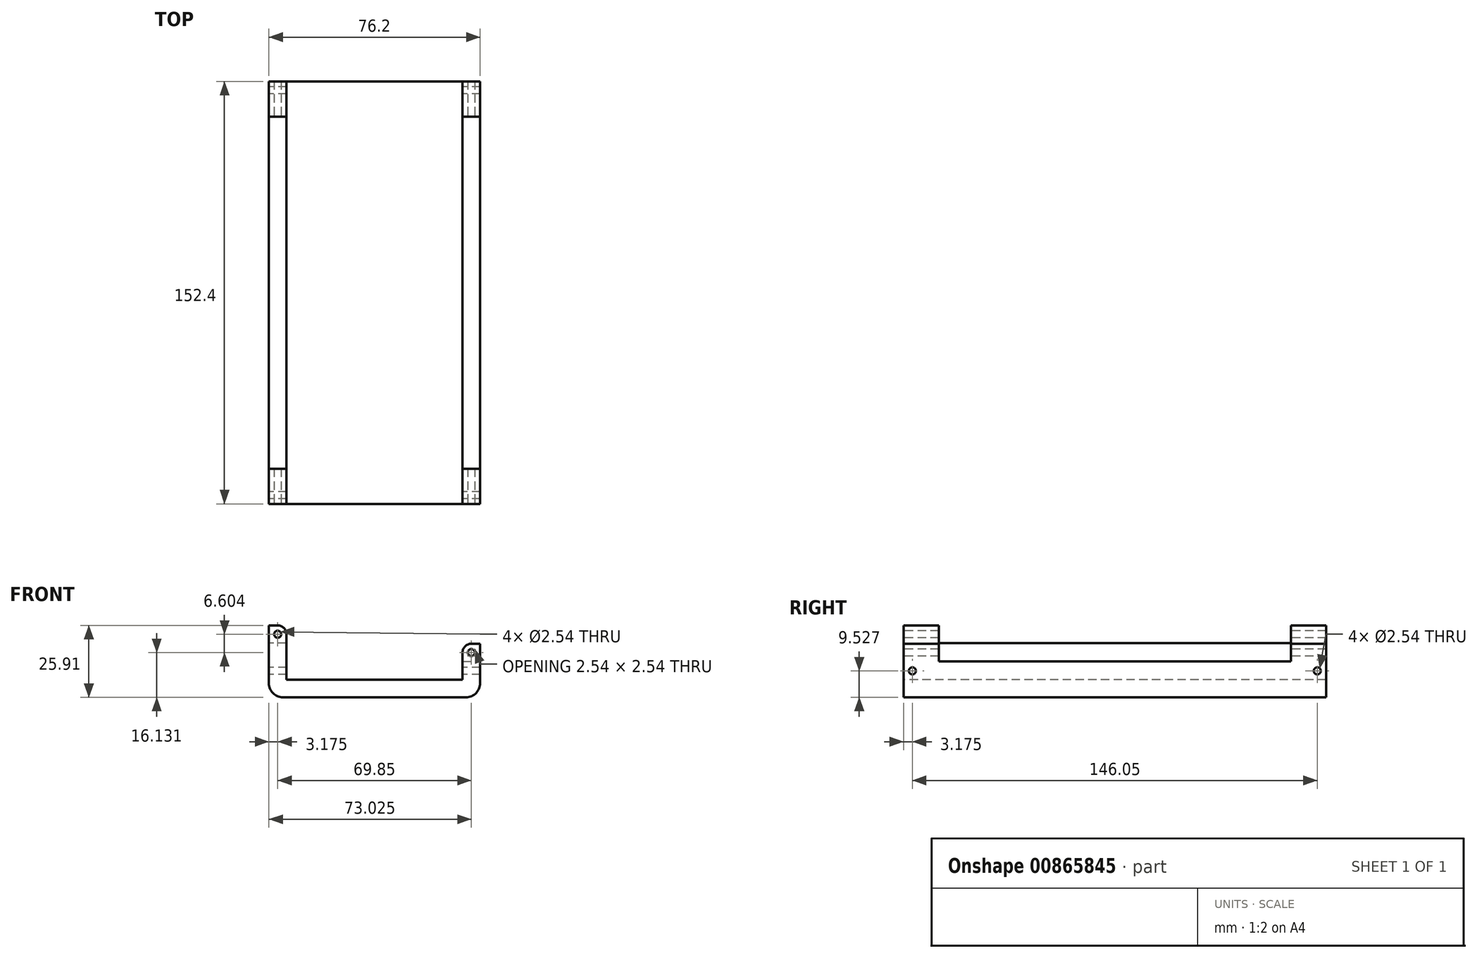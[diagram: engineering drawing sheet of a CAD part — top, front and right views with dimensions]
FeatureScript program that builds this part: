
annotation { "Feature Type Name" : "Feature", "Feature Type Description" : "" }
export const myFeature = defineFeature(function(context is Context, id is Id, definition is map)
    precondition{}
    {
        {
            var Q0;
            Q0=qCreatedBy(makeId("Front.planeOp"),FACE);
            var sketch = newSketch(context, id + "F0", { "sketchPlane" : qUnion([Q0])});
            skLineSegment(sketch, "E0", {"start": v(0, -19.56) * mm, "end": v(0, 0) * mm});
            skLineSegment(sketch, "E1", {"start": v(0, 0) * mm, "end": v(6.35, 0) * mm});
            skLineSegment(sketch, "E2", {"start": v(6.35, 0) * mm, "end": v(6.35, -13.2) * mm});
            skLineSegment(sketch, "E3", {"start": v(6.35, -13.2) * mm, "end": v(69.85, -13.2) * mm});
            skLineSegment(sketch, "E4", {"start": v(69.85, -13.2) * mm, "end": v(69.85, -6.6) * mm});
            skLineSegment(sketch, "E5", {"start": v(69.85, -6.6) * mm, "end": v(76.2, -6.6) * mm});
            skLineSegment(sketch, "E6", {"start": v(76.2, -6.6) * mm, "end": v(76.2, -19.56) * mm});
            skLineSegment(sketch, "E7", {"start": v(0, -19.56) * mm, "end": v(76.2, -19.56) * mm});
            skSolve(sketch);
        }
        {
            var Q0;
            Q0=makeQuery(id+"F0.imprint","IMPRINT",FACE,{"disambiguationData":[TD([[makeQuery(id+"F0.imprint","IMPRINT",EDGE,{"derivedFrom":sQuery(id+"F0.wireOp",EDGE,"E0")}),-1.0]])]});
            extrude(context, id + "F1", {"entities" : qUnion([Q0]), "oppositeDirection" : true, "depth" : 152.4 * mm, "offsetDistance" : 25.4 * mm});
        }
        {
            var Q0;
            Q0=makeQuery(id+"F1.opExtrude","SWEPT_EDGE",EDGE,{"disambiguationData":[OSD([sQuery(id+"F0.wireOp",EDGE,"E0"),sQuery(id+"F0.wireOp",EDGE,"E7")])]});
            var Q1;
            Q1=makeQuery(id+"F1.opExtrude","SWEPT_EDGE",EDGE,{"disambiguationData":[OSD([sQuery(id+"F0.wireOp",EDGE,"E6"),sQuery(id+"F0.wireOp",EDGE,"E7")])]});
            fillet(context, id + "F2", {"entities" : qUnion([Q0, Q1]), "radius" : 5.08 * mm, "tangentPropagation" : true, "allowEdgeOverflow" : false});
        }
        {
            var Q0;
            Q0=makeQuery(id+"F1.opExtrude","SWEPT_FACE",FACE,{"disambiguationData":[OSD([sQuery(id+"F0.wireOp",EDGE,"E3")])]});
            var sketch = newSketch(context, id + "F3", { "sketchPlane" : qUnion([Q0])});
            skLineSegment(sketch, "E8", {"start": v(6.35, 6.35) * mm, "end": v(69.85, 6.35) * mm});
            skLineSegment(sketch, "E9", {"start": v(6.35, 146.05) * mm, "end": v(69.85, 146.05) * mm});
            skLineSegment(sketch, "E10", {"start": v(12.7, 146.05) * mm, "end": v(12.7, 6.35) * mm});
            skLineSegment(sketch, "E11", {"start": v(38.1, 146.05) * mm, "end": v(38.1, 6.35) * mm, "construction": true});
            skLineSegment(sketch, "E12.MirrorCS", {"start": v(63.5, 146.05) * mm, "end": v(63.5, 6.35) * mm});
            skLineSegment(sketch, "E13", {"start": v(12.7, 76.2) * mm, "end": v(63.5, 76.2) * mm, "construction": true});
            skSolve(sketch);
        }
        {
            var Q0;
            Q0=makeQuery(id+"F1.opExtrude","SWEPT_FACE",FACE,{"disambiguationData":[OSD([sQuery(id+"F0.wireOp",EDGE,"E0")])]});
            var sketch = newSketch(context, id + "F4", { "sketchPlane" : qUnion([Q0])});
            skCircle(sketch, "E14", {"center": v(-149.22, -10.03) * mm, "radius": 1.27 * mm});
            skLineSegment(sketch, "E15", {"start": v(-76.2, -14.48) * mm, "end": v(-76.2, 0) * mm, "construction": true});
            skPoint(sketch, "E15.startSnap0", {"position": v(-76.2, -14.48) * mm});
            skCircle(sketch, "E16.MirrorC", {"center": v(-3.18, -10.03) * mm, "radius": 1.27 * mm});
            skSolve(sketch);
        }
        {
            var Q0;
            Q0 = qSketchRegion(id + "F4", true);
            extrude(context, id + "F5", {"entities" : qUnion([Q0]), "operationType" : NewBodyOperationType.REMOVE, "endBound" : BoundingType.THROUGH_ALL, "oppositeDirection" : true, "depth" : 25.4 * mm, "offsetDistance" : 25.4 * mm});
        }
        {
            var Q0;
            Q0=makeQuery(id+"F1.opExtrude","SWEPT_FACE",FACE,{"disambiguationData":[OSD([sQuery(id+"F0.wireOp",EDGE,"E6")])]});
            var sketch = newSketch(context, id + "F6", { "sketchPlane" : qUnion([Q0])});
            skLineSegment(sketch, "E17.bottom", {"start": v(0, -6.6) * mm, "end": v(12.7, -6.6) * mm});
            skLineSegment(sketch, "E17.top", {"start": v(0, -0.25) * mm, "end": v(12.7, -0.25) * mm});
            skLineSegment(sketch, "E17.left", {"start": v(0, -6.6) * mm, "end": v(0, -0.25) * mm});
            skLineSegment(sketch, "E17.right", {"start": v(12.7, -6.6) * mm, "end": v(12.7, -0.25) * mm});
            skLineSegment(sketch, "E18.bottom", {"start": v(152.4, -6.6) * mm, "end": v(139.7, -6.6) * mm});
            skLineSegment(sketch, "E18.top", {"start": v(152.4, -0.25) * mm, "end": v(139.7, -0.25) * mm});
            skLineSegment(sketch, "E18.left", {"start": v(152.4, -6.6) * mm, "end": v(152.4, -0.25) * mm});
            skLineSegment(sketch, "E18.right", {"start": v(139.7, -6.6) * mm, "end": v(139.7, -0.25) * mm});
            skSolve(sketch);
        }
        {
            var Q0;
            Q0 = qSketchRegion(id + "F6", true);
            extrude(context, id + "F7", {"entities" : qUnion([Q0]), "operationType" : NewBodyOperationType.ADD, "oppositeDirection" : true, "depth" : 6.35 * mm, "offsetDistance" : 25.4 * mm});
        }
        {
            var Q0;
            Q0=makeQuery(id+"F1.opExtrude","SWEPT_FACE",FACE,{"disambiguationData":[OSD([sQuery(id+"F0.wireOp",EDGE,"E0")])]});
            var sketch = newSketch(context, id + "F8", { "sketchPlane" : qUnion([Q0])});
            skLineSegment(sketch, "E19.bottom", {"start": v(-152.4, 0) * mm, "end": v(-139.7, 0) * mm});
            skLineSegment(sketch, "E19.top", {"start": v(-152.4, 6.35) * mm, "end": v(-139.7, 6.35) * mm});
            skLineSegment(sketch, "E19.left", {"start": v(-152.4, 0) * mm, "end": v(-152.4, 6.35) * mm});
            skLineSegment(sketch, "E19.right", {"start": v(-139.7, 0) * mm, "end": v(-139.7, 6.35) * mm});
            skLineSegment(sketch, "E20.bottom", {"start": v(0, 0) * mm, "end": v(-12.7, 0) * mm});
            skLineSegment(sketch, "E20.top", {"start": v(0, 6.35) * mm, "end": v(-12.7, 6.35) * mm});
            skLineSegment(sketch, "E20.left", {"start": v(0, 0) * mm, "end": v(0, 6.35) * mm});
            skLineSegment(sketch, "E20.right", {"start": v(-12.7, 0) * mm, "end": v(-12.7, 6.35) * mm});
            skSolve(sketch);
        }
        {
            var Q0;
            Q0 = qSketchRegion(id + "F8", true);
            extrude(context, id + "F9", {"entities" : qUnion([Q0]), "operationType" : NewBodyOperationType.ADD, "oppositeDirection" : true, "depth" : 6.35 * mm, "offsetDistance" : 25.4 * mm});
        }
        {
            var Q0;
            Q0=makeQuery(id+"F7.boolean.opBoolean","MERGE",FACE,{"derivedFrom":[makeQuery(id+"F1.opExtrude","CAP_FACE",FACE,{"disambiguationData":[OSD([sQuery(id+"F0.wireOp",EDGE,"E0"),sQuery(id+"F0.wireOp",EDGE,"E1"),sQuery(id+"F0.wireOp",EDGE,"E2"),sQuery(id+"F0.wireOp",EDGE,"E3"),sQuery(id+"F0.wireOp",EDGE,"E4"),sQuery(id+"F0.wireOp",EDGE,"E5"),sQuery(id+"F0.wireOp",EDGE,"E6"),sQuery(id+"F0.wireOp",EDGE,"E7")])],"isStart":true}),makeQuery(id+"F7.opExtrude","SWEPT_FACE",FACE,{"disambiguationData":[OSD([sQuery(id+"F6.wireOp",EDGE,"E17.left")])]})]});
            var sketch = newSketch(context, id + "F10", { "sketchPlane" : qUnion([Q0])});
            skCircle(sketch, "E21", {"center": v(73.03, -3.43) * mm, "radius": 1.27 * mm});
            skCircle(sketch, "E22", {"center": v(3.18, 3.18) * mm, "radius": 1.27 * mm});
            skSolve(sketch);
        }
        {
            var Q0;
            Q0 = qSketchRegion(id + "F10", true);
            extrude(context, id + "F11", {"entities" : qUnion([Q0]), "operationType" : NewBodyOperationType.REMOVE, "endBound" : BoundingType.THROUGH_ALL, "oppositeDirection" : true, "depth" : 25.4 * mm, "offsetDistance" : 25.4 * mm});
        }
        {
            var Q0;
            Q0=makeQuery(id+"F7.opExtrude","CAP_EDGE",EDGE,{"disambiguationData":[OSD([sQuery(id+"F6.wireOp",EDGE,"E17.top")])],"isStart":false});
            var Q1;
            Q1=makeQuery(id+"F7.opExtrude","CAP_EDGE",EDGE,{"disambiguationData":[OSD([sQuery(id+"F6.wireOp",EDGE,"E18.top")])],"isStart":false});
            var Q2;
            Q2=makeQuery(id+"F9.opExtrude","CAP_EDGE",EDGE,{"disambiguationData":[OSD([sQuery(id+"F8.wireOp",EDGE,"E20.top")])],"isStart":false});
            var Q3;
            Q3=makeQuery(id+"F9.opExtrude","CAP_EDGE",EDGE,{"disambiguationData":[OSD([sQuery(id+"F8.wireOp",EDGE,"E19.top")])],"isStart":false});
            fillet(context, id + "F12", {"entities" : qUnion([Q0, Q1, Q2, Q3]), "radius" : 3.17 * mm, "tangentPropagation" : true, "allowEdgeOverflow" : false});
        }
    });
